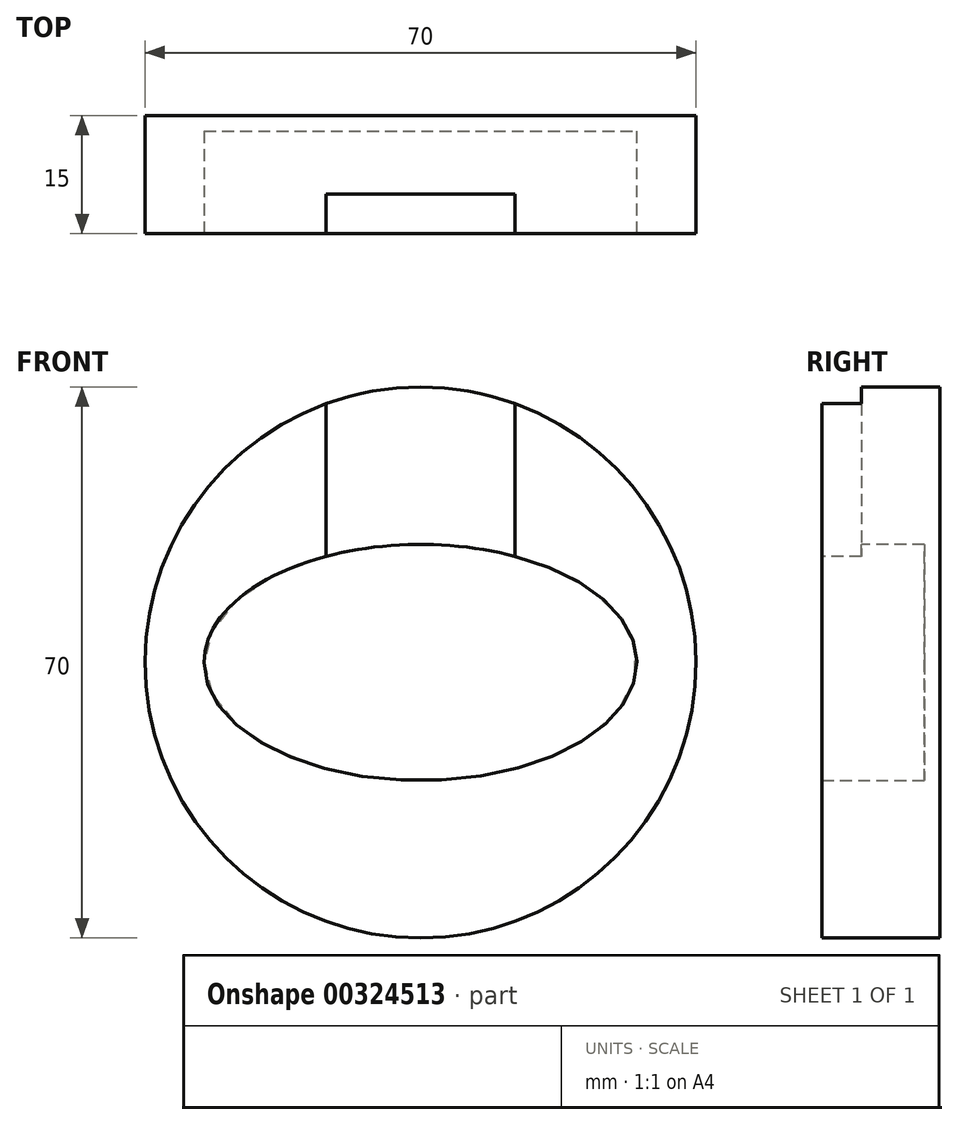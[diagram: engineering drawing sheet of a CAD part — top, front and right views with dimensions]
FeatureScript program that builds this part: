
annotation { "Feature Type Name" : "Feature", "Feature Type Description" : "" }
export const myFeature = defineFeature(function(context is Context, id is Id, definition is map)
    precondition{}
    {
        {
            var Q0;
            Q0=qCreatedBy(makeId("Front.planeOp"),FACE);
            var sketch = newSketch(context, id + "F0", { "sketchPlane" : qUnion([Q0])});
            skCircle(sketch, "E0", {"center": v(0, 0) * mm, "radius": 35 * mm});
            skSolve(sketch);
        }
        {
            var Q0;
            Q0=makeQuery(id+"F0.imprint","IMPRINT",FACE,{"disambiguationData":[TD([[makeQuery(id+"F0.imprint","IMPRINT",EDGE,{"derivedFrom":sQuery(id+"F0.wireOp",EDGE,"E0")}),1.0]])]});
            extrude(context, id + "F1", {"entities" : qUnion([Q0]), "depth" : 15 * mm});
        }
        {
            var Q0;
            Q0=makeQuery(id+"F1.opExtrude","CAP_FACE",FACE,{"disambiguationData":[OSD([sQuery(id+"F0.wireOp",EDGE,"E0")])],"isStart":false});
            var sketch = newSketch(context, id + "F2", { "sketchPlane" : qUnion([Q0])});
            skEllipse(sketch, "E1", {"center": v(0, 0) * mm, "majorRadius": 27.5 * mm, "minorRadius": 15 * mm, "majorAxis": v(-1, 0)});
            skSolve(sketch);
        }
        {
            var Q0;
            Q0=makeQuery(id+"F2.imprint","IMPRINT",FACE,{"disambiguationData":[TD([[makeQuery(id+"F2.imprint","IMPRINT",EDGE,{"derivedFrom":sQuery(id+"F2.wireOp",EDGE,"E1")}),1.0]])]});
            extrude(context, id + "F3", {"entities" : qUnion([Q0]), "operationType" : NewBodyOperationType.REMOVE, "oppositeDirection" : true, "depth" : 13 * mm});
        }
        {
            var Q0;
            Q0=makeQuery(id+"F1.opExtrude","CAP_FACE",FACE,{"disambiguationData":[OSD([sQuery(id+"F0.wireOp",EDGE,"E0")])],"isStart":false});
            var sketch = newSketch(context, id + "F4", { "sketchPlane" : qUnion([Q0])});
            skLineSegment(sketch, "E2.bottom", {"start": v(-12.01, 37.5) * mm, "end": v(11.99, 37.5) * mm});
            skLineSegment(sketch, "E2.top", {"start": v(-12.01, 13.5) * mm, "end": v(11.99, 13.5) * mm});
            skLineSegment(sketch, "E2.left", {"start": v(-12.01, 37.5) * mm, "end": v(-12.01, 13.5) * mm});
            skLineSegment(sketch, "E2.right", {"start": v(11.99, 37.5) * mm, "end": v(11.99, 13.5) * mm});
            skSolve(sketch);
        }
        {
            var Q0;
            Q0 = qSketchRegion(id + "F4", true);
            extrude(context, id + "F5", {"entities" : qUnion([Q0]), "operationType" : NewBodyOperationType.REMOVE, "oppositeDirection" : true, "depth" : 5 * mm});
        }
    });
